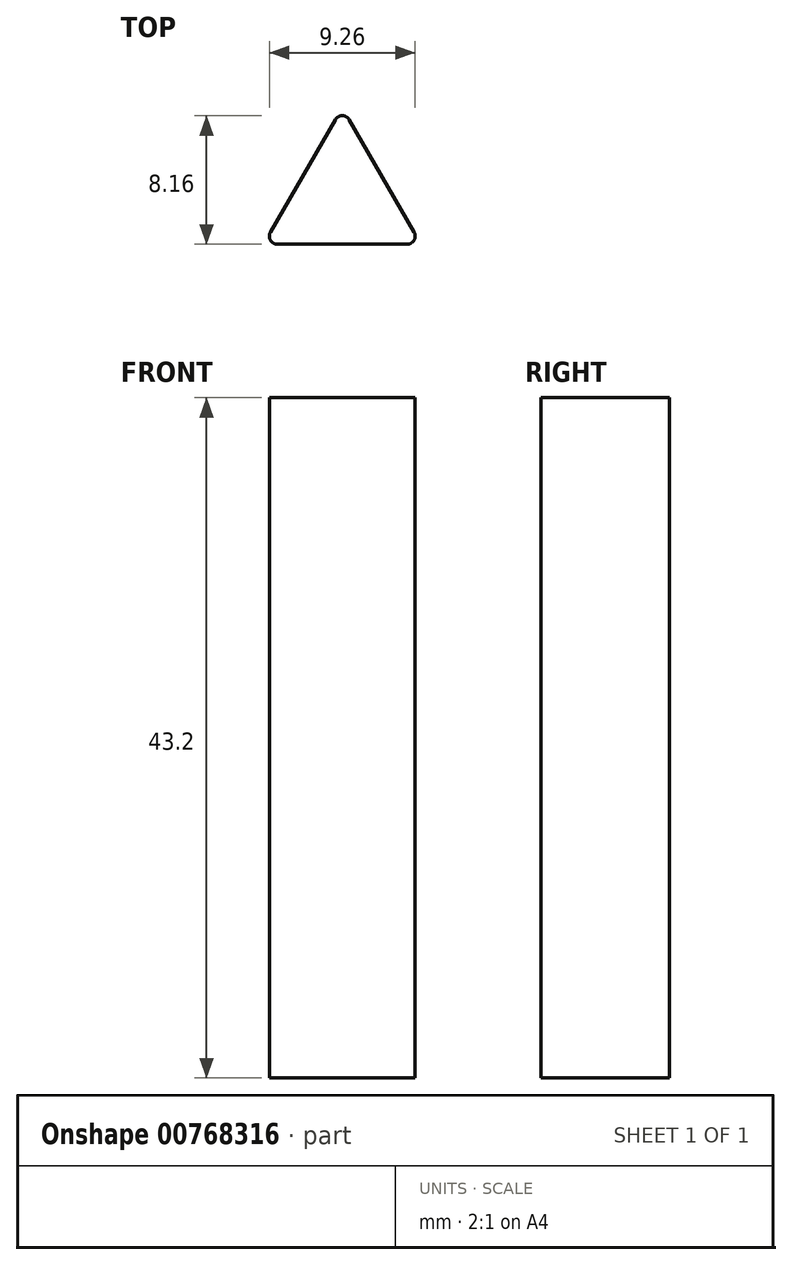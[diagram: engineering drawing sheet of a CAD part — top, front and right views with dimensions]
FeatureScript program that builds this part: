
annotation { "Feature Type Name" : "Feature", "Feature Type Description" : "" }
export const myFeature = defineFeature(function(context is Context, id is Id, definition is map)
    precondition{}
    {
        {
            var Q0;
            Q0=qCreatedBy(makeId("Top.planeOp"),FACE);
            var sketch = newSketch(context, id + "F0", { "sketchPlane" : qUnion([Q0])});
            skCircle(sketch, "E0.cCircle", {"center": v(0, 0) * mm, "radius": 5.77 * mm, "construction": true});
            skLineSegment(sketch, "E0.0", {"start": v(0.43, 5.02) * mm, "end": v(4.57, -2.14) * mm});
            skLineSegment(sketch, "E0.1", {"start": v(4.13, -2.89) * mm, "end": v(-4.13, -2.89) * mm});
            skLineSegment(sketch, "E0.2", {"start": v(-4.57, -2.14) * mm, "end": v(-0.43, 5.02) * mm});
            skPoint(sketch, "E1.visualSharp", {"position": v(0, 5.77) * mm});
            skArc(sketch, "E1.filletArc", {"start": v(0.43, 5.02) * mm, "mid": v(0, 5.27) * mm, "end": v(-0.43, 5.02) * mm});
            skPoint(sketch, "E2.visualSharp", {"position": v(-5, -2.89) * mm});
            skArc(sketch, "E2.filletArc", {"start": v(-4.57, -2.14) * mm, "mid": v(-4.57, -2.64) * mm, "end": v(-4.13, -2.89) * mm});
            skPoint(sketch, "E3.visualSharp", {"position": v(5, -2.89) * mm});
            skArc(sketch, "E3.filletArc", {"start": v(4.13, -2.89) * mm, "mid": v(4.57, -2.64) * mm, "end": v(4.57, -2.14) * mm});
            skSolve(sketch);
        }
        {
            var Q0;
            Q0=makeQuery(id+"F0.imprint","IMPRINT",FACE,{"disambiguationData":[TD([[makeQuery(id+"F0.imprint","IMPRINT",EDGE,{"derivedFrom":sQuery(id+"F0.wireOp",EDGE,"E0.0")}),-1.0]])]});
            extrude(context, id + "F1", {"entities" : qUnion([Q0]), "depth" : 43.2 * mm, "offsetDistance" : 25 * mm});
        }
    });
